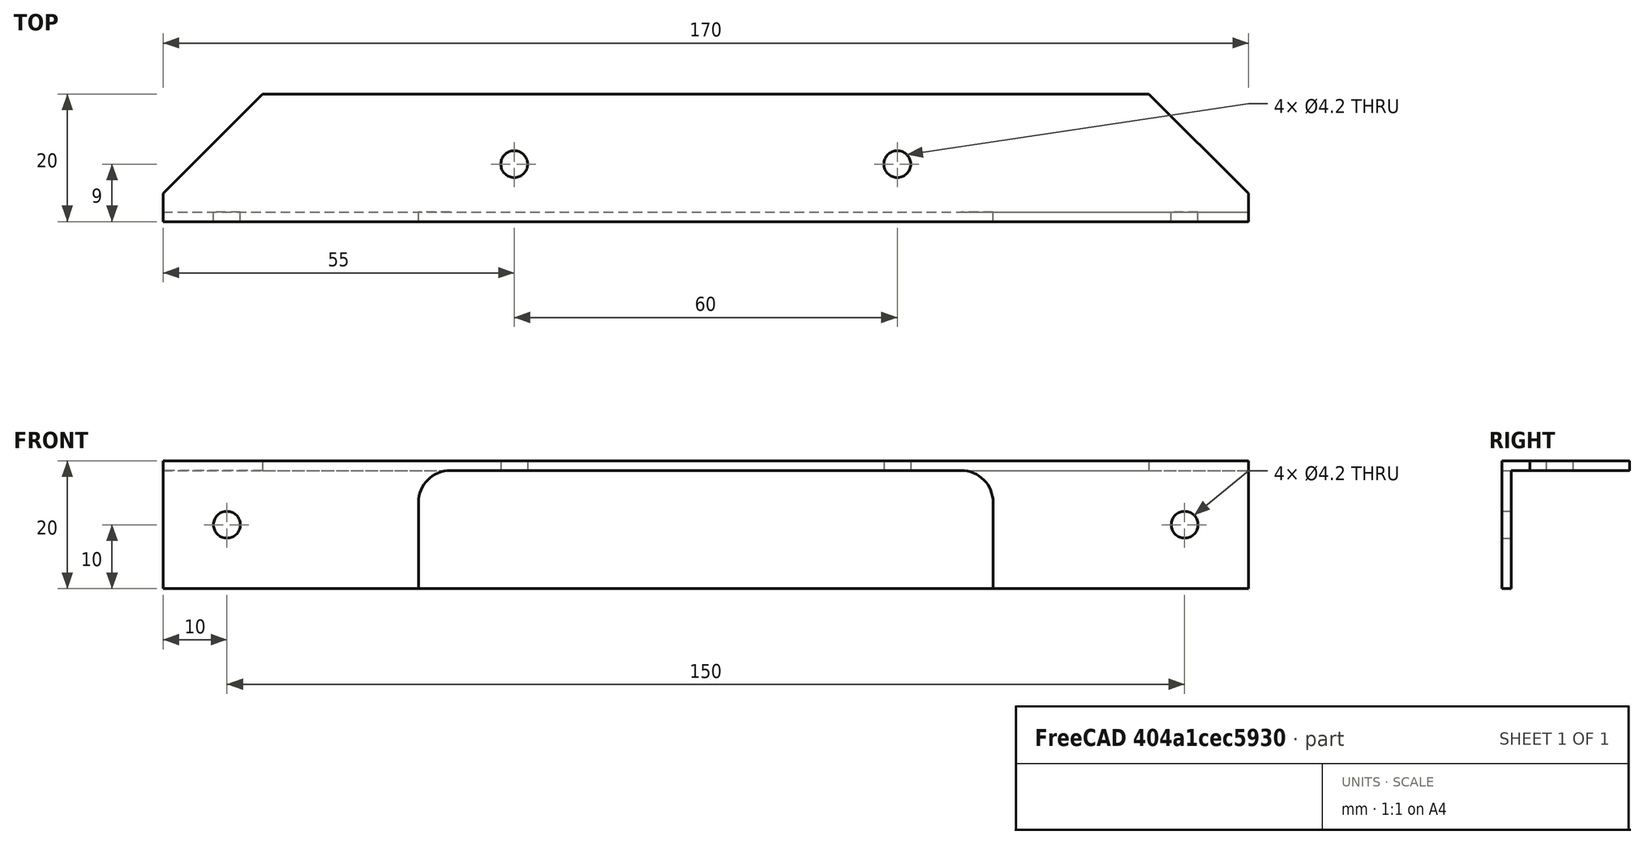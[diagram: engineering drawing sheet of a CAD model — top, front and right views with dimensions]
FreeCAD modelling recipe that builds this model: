
FCSTD DOCUMENT  (FreeCAD 1.0R39319 (Git))
Label: OCT-CPBRC
License: Creative Commons Attribution 4.0
LicenseURL: https://creativecommons.org/licenses/by/4.0/
objects: TechDraw::DrawViewDimension×31, TechDraw::DrawProjGroupItem×6, Sketcher::SketchObject×5, PartDesign::Hole×2, PartDesign::Pocket×2, PartDesign::Body×2, TechDraw::DrawSVGTemplate×2, TechDraw::DrawProjGroup×2, TechDraw::DrawPage×2, PartDesign::Pad×1, PartDesign::FeatureBase×1
note: 80 computed .brp shape members not serialized (recipe doc carries the construction recipe); baked Part::Feature solids carry a one-line shape summary decoded from their .brp

FEATURE [Sketcher::SketchObject] Sketch
  ArcFitTolerance = 1e-06
  AttachmentSupport = -> [YZ_Plane]
  FullyConstrained = true
  MakeInternals = false
  MapMode = 5
  Placement = pos=(0,0,0) rot=(0.57735,0.57735,0.57735;2.0944rad)
  sketch-geometry (6):
    g0: LineSegment StartX=0 StartY=0 StartZ=0 EndX=0 EndY=20 EndZ=0
    g1: LineSegment StartX=0 StartY=20 StartZ=0 EndX=20 EndY=20 EndZ=0
    g2: LineSegment StartX=20 StartY=20 StartZ=0 EndX=20 EndY=18.5 EndZ=0
    g3: LineSegment StartX=20 StartY=18.5 StartZ=0 EndX=1.5 EndY=18.5 EndZ=0
    g4: LineSegment StartX=1.5 StartY=18.5 StartZ=0 EndX=1.5 EndY=0 EndZ=0
    g5: LineSegment StartX=1.5 StartY=0 StartZ=0 EndX=0 EndY=0 EndZ=0
  constraints (17):
    c: Coincident(g-1,g0)
    c: PointOnObject(g0,g-2)
    c: Coincident(g0,g1)
    c: Horizontal(g1)
    c: Coincident(g1,g2)
    c: Coincident(g2,g3)
    c: Horizontal(g3)
    c: Coincident(g3,g4)
    c: PointOnObject(g4,g-1)
    c: Vertical(g4)
    c: Coincident(g4,g5)
    c: Coincident(g5,g0)
    c: Vertical(g2)
    c: DistanceY(g0,g0) = 20
    c: DistanceY(g2,g2) = 1.5
    c: Equal(g5,g2)
    c: DistanceX(g1,g1) = 20
FEATURE [PartDesign::Pad] Pad
  Direction = (1,0,0)
  Length = 170
  Length2 = 10
  Midplane = true
  Placement = pos=(0,0,0) rot=(1,1,1;2.0944rad)
  Profile = -> Sketch
  ReferenceAxis = -> Sketch [N_Axis]
  Suppressed = false
  Type = 0
FEATURE [Sketcher::SketchObject] Sketch001
  ArcFitTolerance = 1e-06
  AttachmentSupport = -> [Pad]
  FullyConstrained = true
  MakeInternals = false
  MapMode = 5
  Placement = pos=(0,2e-16,0) rot=(0.57735,0.57735,-0.57735;2.0944rad)
  sketch-geometry (3):
    g0: Circle CenterX=-10 CenterY=-75 CenterZ=0 NormalX=0 NormalY=0 NormalZ=1 AngleXU=0 Radius=2
    g1: Circle CenterX=-10 CenterY=75 CenterZ=0 NormalX=0 NormalY=0 NormalZ=1 AngleXU=0 Radius=2
    g2: LineSegment [constr] StartX=-10 StartY=-75 StartZ=0 EndX=-10 EndY=75 EndZ=0
  constraints (7):
    c: Coincident(g2,g0)
    c: Coincident(g2,g1)
    c: DistanceY(g2,g2) = 150
    c: Equal(g0,g1)
    c: Diameter(g0) = 4
    c: Distance(g0,g-2) = 10
    c: Symmetric(g0,g1,g-1)
FEATURE [PartDesign::Hole] Hole
  BaseFeature = -> Pad
  CustomThreadClearance = 0
  Depth = 348.12
  DepthType = 1
  Diameter = 4.2
  DrillForDepth = false
  DrillPoint = 1
  DrillPointAngle = 118
  HoleCutCountersinkAngle = 90
  HoleCutCustomValues = false
  HoleCutDepth = 0
  HoleCutDiameter = 6.1
  HoleCutType = 0
  ModelThread = false
  Placement = pos=(0,0,0) rot=(1,1,1;2.0944rad)
  Profile = -> Sketch001
  Suppressed = false
  Tapered = false
  TaperedAngle = 90
  ThreadClass = 0
  ThreadDepth = 348.12
  ThreadDepthType = 0
  ThreadDirection = 0
  ThreadFit = 0
  ThreadSize = 0
  ThreadType = 0
  Threaded = false
  UseCustomThreadClearance = false
FEATURE [Sketcher::SketchObject] Sketch002
  ArcFitTolerance = 1e-06
  AttachmentSupport = -> [Hole]
  FullyConstrained = true
  MakeInternals = false
  MapMode = 5
  Placement = pos=(0,4.4e-15,20) rot=(0,0,-1;1.5708rad)
  sketch-geometry (3):
    g0: Circle CenterX=-9 CenterY=30 CenterZ=0 NormalX=0 NormalY=0 NormalZ=1 AngleXU=0 Radius=2
    g1: Circle CenterX=-9 CenterY=-30 CenterZ=0 NormalX=0 NormalY=0 NormalZ=1 AngleXU=0 Radius=2
    g2: LineSegment [constr] StartX=-9 StartY=30 StartZ=0 EndX=-9 EndY=-30 EndZ=0
  constraints (7):
    c: Coincident(g2,g0)
    c: Coincident(g2,g1)
    c: Symmetric(g1,g0,g-1)
    c: Equal(g0,g1)
    c: Diameter(g1) = 4
    c: DistanceY(g2,g2) = 60
    c: DistanceX(g0,g-1) = 9
FEATURE [PartDesign::Hole] Hole001
  BaseFeature = -> Hole
  CustomThreadClearance = 0
  Depth = 348.12
  DepthType = 1
  Diameter = 4.2
  DrillForDepth = false
  DrillPoint = 1
  DrillPointAngle = 118
  HoleCutCountersinkAngle = 90
  HoleCutCustomValues = false
  HoleCutDepth = 0
  HoleCutDiameter = 6.1
  HoleCutType = 0
  ModelThread = false
  Placement = pos=(0,0,0) rot=(1,1,1;2.0944rad)
  Profile = -> Sketch002
  Suppressed = false
  Tapered = false
  TaperedAngle = 90
  ThreadClass = 0
  ThreadDepth = 348.12
  ThreadDepthType = 0
  ThreadDirection = 0
  ThreadFit = 0
  ThreadSize = 0
  ThreadType = 0
  Threaded = false
  UseCustomThreadClearance = false
FEATURE [Sketcher::SketchObject] Sketch003
  ArcFitTolerance = 1e-06
  AttachmentSupport = -> [Hole001]
  ExternalGeometry = -> [Hole001]
  FullyConstrained = true
  MakeInternals = false
  MapMode = 5
  Placement = pos=(0,4.4e-15,20) rot=(0,0,-1;1.5708rad)
  sketch-geometry (6):
    g0: LineSegment StartX=-4.4 StartY=85 StartZ=0 EndX=-20 EndY=85 EndZ=0
    g1: LineSegment StartX=-20 StartY=85 StartZ=0 EndX=-20 EndY=69.4 EndZ=0
    g2: LineSegment StartX=-20 StartY=69.4 StartZ=0 EndX=-4.4 EndY=85 EndZ=0
    g3: LineSegment StartX=-4.4 StartY=-85 StartZ=0 EndX=-20 EndY=-85 EndZ=0
    g4: LineSegment StartX=-20 StartY=-85 StartZ=0 EndX=-20 EndY=-69.4 EndZ=0
    g5: LineSegment StartX=-20 StartY=-69.4 StartZ=0 EndX=-4.4 EndY=-85 EndZ=0
  constraints (16):
    c: Horizontal(g0)
    c: Coincident(g0,g1)
    c: Vertical(g1)
    c: Coincident(g1,g2)
    c: Coincident(g2,g0)
    c: Horizontal(g3)
    c: Coincident(g3,g4)
    c: Coincident(g4,g5)
    c: Coincident(g5,g3)
    c: Vertical(g4)
    c: Equal(g4,g3)
    c: Equal(g1,g0)
    c: Equal(g1,g4)
    c: Coincident(g0,g-3)
    c: DistanceX(g0,g-3) = 4.4
    c: Symmetric(g0,g3,g-1)
FEATURE [PartDesign::Pocket] Pocket
  BaseFeature = -> Hole001
  Direction = (0,0,-1)
  Length = 5
  Length2 = 5
  Placement = pos=(0,0,0) rot=(1,1,1;2.0944rad)
  Profile = -> Sketch003
  ReferenceAxis = -> Sketch003 [N_Axis]
  Suppressed = false
  Type = 2
FEATURE [PartDesign::Body] Body  label="OCT-CPBRC-AA"
  AllowCompound = false
  Group = -> [Sketch,Pad,Sketch001,Hole,Sketch002,Hole001,Sketch003,Pocket]
  Origin = -> Origin
  Tip = -> Pocket
FEATURE [TechDraw::DrawSVGTemplate] Template
  EditableTexts = approval_person=S. Aphelion; creator=Michael Stoll; date_of_issue=13/02/2026; document_status=In preparation; document_type=Component Drawing; drawing_number=DN; general_tolerances=+-0.1 mm; language_code=EN; part_material=Aluminium; responsible_department=RD; revision_index=A; scale=1 : 1; sheet_number=1 / 1; supplementary_title_1=Chamber Top Bracket; title=OCT-CPBRC-AA
  Height = 297
  Orientation = 1
  Template = C:/Program Files/FreeCAD 1.0/data/Mod/TechDraw/Templates/A3_Landscape_ISO5457_advanced.svg
  Width = 420
FEATURE [TechDraw::DrawProjGroupItem] View  label="Front"
  CoarseView = false
  Direction = (0,-1,0)
  Focus = 100
  HardHidden = false
  IsoCount = 0
  IsoHidden = false
  IsoVisible = false
  LockPosition = true
  Perspective = false
  Rotation = 0
  RotationVector = (1,0,0)
  ScaleType = 2
  ScrubCount = 1
  SeamHidden = false
  SeamVisible = false
  SmoothHidden = false
  SmoothVisible = true
  Source = -> [Body]
  Type = 0
  X = 0
  XDirection = (1,0,0)
  Y = 0
FEATURE [TechDraw::DrawProjGroupItem] ProjItem  label="Top"
  CoarseView = false
  Direction = (0,0,1)
  Focus = 100
  HardHidden = false
  IsoCount = 0
  IsoHidden = false
  IsoVisible = false
  LockPosition = false
  Perspective = false
  Rotation = 0
  RotationVector = (1,0,0)
  ScaleType = 0
  ScrubCount = 1
  SeamHidden = false
  SeamVisible = false
  SmoothHidden = false
  SmoothVisible = true
  Source = -> [Body]
  Type = 4
  X = 0
  XDirection = (1,0,0)
  Y = 70
FEATURE [TechDraw::DrawProjGroupItem] ProjItem001  label="Right"
  CoarseView = false
  Direction = (1,-1e-16,0)
  Focus = 100
  HardHidden = false
  IsoCount = 0
  IsoHidden = false
  IsoVisible = false
  LockPosition = false
  Perspective = false
  Rotation = 0
  RotationVector = (1,0,0)
  ScaleType = 0
  ScrubCount = 1
  SeamHidden = false
  SeamVisible = false
  SmoothHidden = false
  SmoothVisible = true
  Source = -> [Body]
  Type = 2
  X = 145
  XDirection = (1e-16,1,0)
  Y = 0
FEATURE [TechDraw::DrawProjGroup] ProjGroup
  Anchor = -> View
  AutoDistribute = true
  LockPosition = false
  ProjectionType = 1
  Rotation = 0
  ScaleType = 0
  Source = -> [Body]
  Views = -> [View,ProjItem,ProjItem001]
  X = 185.7
  Y = 128.889
  spacingX = 50
  spacingY = 50
FEATURE [TechDraw::DrawViewDimension] Dimension
  AngleOverride = false
  Arbitrary = false
  ArbitraryTolerances = false
  BoxCorners = (2) [(-10,-10,0),(10,10,0)]
  EqualTolerance = true
  ExtensionAngle = 0
  FormatSpec = %.1f
  FormatSpecOverTolerance = %+.1f
  FormatSpecUnderTolerance = %+.1f
  Inverted = false
  LineAngle = 0
  LockPosition = false
  MeasureType = 1
  OverTolerance = 0
  References2D = -> [ProjItem001]
  Rotation = 0
  ScaleType = 0
  TheoreticalExact = false
  Type = 2
  UnderTolerance = 0
  X = -31.2542
  Y = 0
FEATURE [TechDraw::DrawViewDimension] Dimension001
  AngleOverride = false
  Arbitrary = false
  ArbitraryTolerances = false
  BoxCorners = (2) [(-10,-10,0),(10,10,0)]
  EqualTolerance = true
  ExtensionAngle = 0
  FormatSpec = %.1f
  FormatSpecOverTolerance = %+.1f
  FormatSpecUnderTolerance = %+.1f
  Inverted = false
  LineAngle = 0
  LockPosition = false
  MeasureType = 1
  OverTolerance = 0
  References2D = -> [ProjItem001]
  Rotation = 0
  ScaleType = 0
  TheoreticalExact = false
  Type = 1
  UnderTolerance = 0
  X = 0
  Y = 29.0333
FEATURE [TechDraw::DrawViewDimension] Dimension002
  AngleOverride = false
  Arbitrary = false
  ArbitraryTolerances = false
  BoxCorners = (2) [(-10,-10,0),(10,10,0)]
  EqualTolerance = true
  ExtensionAngle = 0
  FormatSpec = %.1f
  FormatSpecOverTolerance = %+.1f
  FormatSpecUnderTolerance = %+.1f
  Inverted = false
  LineAngle = 0
  LockPosition = false
  MeasureType = 1
  OverTolerance = 0
  References2D = -> [ProjItem001]
  Rotation = 0
  ScaleType = 0
  TheoreticalExact = false
  Type = 0
  UnderTolerance = 0
  X = 13.3418
  Y = 21.504
FEATURE [TechDraw::DrawViewDimension] Dimension003
  AngleOverride = false
  Arbitrary = false
  ArbitraryTolerances = false
  BoxCorners = (2) [(-10,-10,0),(10,10,0)]
  EqualTolerance = true
  ExtensionAngle = 0
  FormatSpec = %.1f
  FormatSpecOverTolerance = %+.1f
  FormatSpecUnderTolerance = %+.1f
  Inverted = false
  LineAngle = 0
  LockPosition = false
  MeasureType = 1
  OverTolerance = 0
  References2D = -> [ProjItem001]
  Rotation = 0
  ScaleType = 0
  TheoreticalExact = false
  Type = 0
  UnderTolerance = 0
  X = -22.9044
  Y = -14.5718
FEATURE [TechDraw::DrawViewDimension] Dimension004
  AngleOverride = false
  Arbitrary = false
  ArbitraryTolerances = false
  BoxCorners = (2) [(-85,-10,0),(85,10,0)]
  EqualTolerance = true
  ExtensionAngle = 0
  FormatSpec = %.1f
  FormatSpecOverTolerance = %+.1f
  FormatSpecUnderTolerance = %+.1f
  Inverted = false
  LineAngle = 0
  LockPosition = false
  MeasureType = 1
  OverTolerance = 0
  References2D = -> [ProjItem]
  Rotation = 0
  ScaleType = 0
  TheoreticalExact = false
  Type = 1
  UnderTolerance = 0
  X = 0
  Y = -21.4245
FEATURE [TechDraw::DrawViewDimension] Dimension005
  AngleOverride = false
  Arbitrary = false
  ArbitraryTolerances = false
  BoxCorners = (2) [(-85,-10,0),(85,10,0)]
  EqualTolerance = true
  ExtensionAngle = 0
  FormatSpec = %.1f
  FormatSpecOverTolerance = %+.1f
  FormatSpecUnderTolerance = %+.1f
  Inverted = false
  LineAngle = 0
  LockPosition = false
  MeasureType = 1
  OverTolerance = 0
  References2D = -> [ProjItem]
  Rotation = 0
  ScaleType = 0
  TheoreticalExact = false
  Type = 2
  UnderTolerance = 0
  X = -106.361
  Y = -7.8
FEATURE [TechDraw::DrawViewDimension] Dimension006
  AngleOverride = false
  Arbitrary = false
  ArbitraryTolerances = false
  BoxCorners = (2) [(-85,-10,0),(85,10,0)]
  EqualTolerance = true
  ExtensionAngle = 0
  FormatSpec = %.1f
  FormatSpecOverTolerance = %+.1f
  FormatSpecUnderTolerance = %+.1f
  Inverted = false
  LineAngle = 0
  LockPosition = false
  MeasureType = 1
  OverTolerance = 0
  References2D = -> [ProjItem]
  Rotation = 0
  ScaleType = 0
  TheoreticalExact = false
  Type = 6
  UnderTolerance = 0
  X = -77.4669
  Y = 20.3711
FEATURE [TechDraw::DrawViewDimension] Dimension007
  AngleOverride = false
  Arbitrary = false
  ArbitraryTolerances = false
  BoxCorners = (2) [(-85,-10,0),(85,10,0)]
  EqualTolerance = true
  ExtensionAngle = 0
  FormatSpec = %.1f
  FormatSpecOverTolerance = %+.1f
  FormatSpecUnderTolerance = %+.1f
  Inverted = false
  LineAngle = 0
  LockPosition = false
  MeasureType = 1
  OverTolerance = 0
  References2D = -> [ProjItem]
  Rotation = 0
  ScaleType = 0
  TheoreticalExact = false
  Type = 0
  UnderTolerance = 0
  X = 57.5
  Y = 30.1612
FEATURE [TechDraw::DrawViewDimension] Dimension008
  AngleOverride = false
  Arbitrary = false
  ArbitraryTolerances = false
  BoxCorners = (2) [(-85,-10,0),(85,10,0)]
  EqualTolerance = true
  ExtensionAngle = 0
  FormatSpec = %.1f
  FormatSpecOverTolerance = %+.1f
  FormatSpecUnderTolerance = %+.1f
  Inverted = false
  LineAngle = 0
  LockPosition = false
  MeasureType = 1
  OverTolerance = 0
  References2D = -> [ProjItem]
  Rotation = 0
  ScaleType = 0
  TheoreticalExact = false
  Type = 1
  UnderTolerance = 0
  X = 0
  Y = 30.1612
FEATURE [TechDraw::DrawViewDimension] Dimension009
  AngleOverride = false
  Arbitrary = false
  ArbitraryTolerances = false
  BoxCorners = (2) [(-85,-10,0),(85,10,0)]
  EqualTolerance = true
  ExtensionAngle = 0
  FormatSpec = %.1f
  FormatSpecOverTolerance = %+.1f
  FormatSpecUnderTolerance = %+.1f
  Inverted = false
  LineAngle = 0
  LockPosition = false
  MeasureType = 1
  OverTolerance = 0
  References2D = -> [View]
  Rotation = 0
  ScaleType = 0
  TheoreticalExact = false
  Type = 0
  UnderTolerance = 0
  X = 80
  Y = 29.1973
FEATURE [TechDraw::DrawViewDimension] Dimension010
  AngleOverride = false
  Arbitrary = false
  ArbitraryTolerances = false
  BoxCorners = (2) [(-85,-10,0),(85,10,0)]
  EqualTolerance = true
  ExtensionAngle = 0
  FormatSpec = %.1f
  FormatSpecOverTolerance = %+.1f
  FormatSpecUnderTolerance = %+.1f
  Inverted = false
  LineAngle = 0
  LockPosition = false
  MeasureType = 1
  OverTolerance = 0
  References2D = -> [View]
  Rotation = 0
  ScaleType = 0
  TheoreticalExact = false
  Type = 1
  UnderTolerance = 0
  X = 0
  Y = 29.1973
FEATURE [TechDraw::DrawViewDimension] Dimension011
  AngleOverride = false
  Arbitrary = false
  ArbitraryTolerances = false
  BoxCorners = (2) [(-85,-10,0),(85,10,0)]
  EqualTolerance = true
  ExtensionAngle = 0
  FormatSpec = %.1f
  FormatSpecOverTolerance = %+.1f
  FormatSpecUnderTolerance = %+.1f
  Inverted = false
  LineAngle = 0
  LockPosition = false
  MeasureType = 1
  OverTolerance = 0
  References2D = -> [ProjItem]
  Rotation = 0
  ScaleType = 0
  TheoreticalExact = false
  Type = 0
  UnderTolerance = 0
  X = 115.395
  Y = -5.5
FEATURE [TechDraw::DrawViewDimension] Dimension012
  AngleOverride = false
  Arbitrary = false
  ArbitraryTolerances = false
  BoxCorners = (2) [(-85,-10,0),(85,10,0)]
  EqualTolerance = true
  ExtensionAngle = 0
  FormatSpec = %.1f
  FormatSpecOverTolerance = %+.1f
  FormatSpecUnderTolerance = %+.1f
  Inverted = false
  LineAngle = 0
  LockPosition = false
  MeasureType = 1
  OverTolerance = 0
  References2D = -> [View]
  Rotation = 0
  ScaleType = 0
  TheoreticalExact = false
  Type = 0
  UnderTolerance = 0
  X = 106.675
  Y = 5
FEATURE [TechDraw::DrawViewDimension] Dimension013
  AngleOverride = false
  Arbitrary = false
  ArbitraryTolerances = false
  BoxCorners = (2) [(-85,-10,0),(85,10,0)]
  EqualTolerance = true
  ExtensionAngle = 0
  FormatSpec = ⌀%.1f
  FormatSpecOverTolerance = %+.1f
  FormatSpecUnderTolerance = %+.1f
  Inverted = false
  LineAngle = 0
  LockPosition = false
  MeasureType = 1
  OverTolerance = 0
  References2D = -> [ProjItem]
  Rotation = 0
  ScaleType = 0
  TheoreticalExact = false
  Type = 5
  UnderTolerance = 0
  X = -51.1959
  Y = 35.4634
FEATURE [TechDraw::DrawViewDimension] Dimension014
  AngleOverride = false
  Arbitrary = false
  ArbitraryTolerances = false
  BoxCorners = (2) [(-85,-10,0),(85,10,0)]
  EqualTolerance = true
  ExtensionAngle = 0
  FormatSpec = ⌀%.1f
  FormatSpecOverTolerance = %+.1f
  FormatSpecUnderTolerance = %+.1f
  Inverted = false
  LineAngle = 0
  LockPosition = false
  MeasureType = 1
  OverTolerance = 0
  References2D = -> [View]
  Rotation = 0
  ScaleType = 0
  TheoreticalExact = false
  Type = 5
  UnderTolerance = 0
  X = -114.095
  Y = -17.0735
FEATURE [TechDraw::DrawPage] Page  label="AA"
  KeepUpdated = true
  NextBalloonIndex = 1
  ProjectionType = 1
  Template = -> Template
  Views = -> [ProjGroup,Dimension,Dimension001,Dimension002,Dimension003,Dimension004,Dimension005,Dimension006,Dimension007,Dimension008,Dimension009,Dimension010,Dimension011,Dimension012,Dimension013,Dimension014]
FEATURE [PartDesign::FeatureBase] Clone
  BaseFeature = -> Pocket
  Placement = pos=(0,0,0) rot=(1,1,1;2.0944rad)
  Suppressed = false
FEATURE [Sketcher::SketchObject] Sketch004
  ArcFitTolerance = 1e-06
  AttachmentSupport = -> [XZ_Plane002]
  ExternalGeometry = -> [Clone]
  FullyConstrained = true
  MakeInternals = false
  MapMode = 5
  Placement = pos=(0,0,0) rot=(1,0,0;1.5708rad)
  sketch-geometry (6):
    g0: ArcOfCircle CenterX=-40 CenterY=13.5 CenterZ=0 NormalX=0 NormalY=0 NormalZ=1 AngleXU=0 Radius=5 StartAngle=1.5708 EndAngle=3.14159
    g1: ArcOfCircle CenterX=40 CenterY=13.5 CenterZ=0 NormalX=0 NormalY=0 NormalZ=1 AngleXU=0 Radius=5 StartAngle=0 EndAngle=1.5708
    g2: LineSegment StartX=-40 StartY=18.5 StartZ=0 EndX=40 EndY=18.5 EndZ=0
    g3: LineSegment StartX=-45 StartY=13.5 StartZ=0 EndX=-45 EndY=0 EndZ=0
    g4: LineSegment StartX=-45 StartY=0 StartZ=0 EndX=45 EndY=0 EndZ=0
    g5: LineSegment StartX=45 StartY=0 StartZ=0 EndX=45 EndY=13.5 EndZ=0
  constraints (15):
    c: Tangent(g0,g3) = -1.5708
    c: Coincident(g3,g4)
    c: Horizontal(g4)
    c: Coincident(g4,g5)
    c: Vertical(g5)
    c: Vertical(g3)
    c: Tangent(g2,g0) = 1.5708
    c: Tangent(g5,g1) = -1.5708
    c: Tangent(g2,g1) = 1.5708
    c: Symmetric(g0,g1,g-2)
    c: Equal(g0,g1)
    c: Radius(g0) = 5
    c: PointOnObject(g-3,g2)
    c: PointOnObject(g4,g-1)
    c: DistanceX(g4,g4) = 90
FEATURE [PartDesign::Pocket] Pocket001
  BaseFeature = -> Clone
  Direction = (0,1,-2e-16)
  Length = 5
  Length2 = 5
  Placement = pos=(0,0,0) rot=(1,1,1;2.0944rad)
  Profile = -> Sketch004
  ReferenceAxis = -> Sketch004 [N_Axis]
  Suppressed = false
  Type = 2
FEATURE [PartDesign::Body] Body002  label="OCT-CPBRC-BA"
  AllowCompound = false
  Group = -> [Clone,Sketch004,Pocket001]
  Origin = -> Origin002
  Tip = -> Pocket001
FEATURE [TechDraw::DrawSVGTemplate] Template001
  EditableTexts = approval_person=S. Aphelion; creator=Michael Stoll; date_of_issue=13/02/2026; document_status=In preparation; document_type=Component Drawing; drawing_number=DN; general_tolerances=ISO 2768-m; language_code=EN; part_material=Aluminium; responsible_department=RD; revision_index=A; scale=1 : 1; sheet_number=2 / 2; supplementary_title_1=Chamber Top Bracket, Hinge; title=OCT-CPBRC-BA
  Height = 297
  Orientation = 1
  Template = C:/Program Files/FreeCAD 1.0/data/Mod/TechDraw/Templates/A3_Landscape_ISO5457_advanced.svg
  Width = 420
FEATURE [TechDraw::DrawProjGroupItem] View001  label="Front001"
  CoarseView = false
  Direction = (0,-1,0)
  Focus = 100
  HardHidden = false
  IsoCount = 0
  IsoHidden = false
  IsoVisible = false
  LockPosition = true
  Perspective = false
  Rotation = 0
  RotationVector = (1,0,0)
  ScaleType = 2
  ScrubCount = 1
  SeamHidden = false
  SeamVisible = false
  SmoothHidden = false
  SmoothVisible = true
  Source = -> [Body002]
  Type = 0
  X = 0
  XDirection = (1,0,0)
  Y = 0
FEATURE [TechDraw::DrawProjGroupItem] ProjItem002  label="Top001"
  CoarseView = false
  Direction = (0,0,1)
  Focus = 100
  HardHidden = false
  IsoCount = 0
  IsoHidden = false
  IsoVisible = false
  LockPosition = false
  Perspective = false
  Rotation = 0
  RotationVector = (1,0,0)
  ScaleType = 0
  ScrubCount = 1
  SeamHidden = false
  SeamVisible = false
  SmoothHidden = false
  SmoothVisible = true
  Source = -> [Body002]
  Type = 4
  X = 0
  XDirection = (1,0,0)
  Y = 70
FEATURE [TechDraw::DrawProjGroupItem] ProjItem003  label="Right001"
  CoarseView = false
  Direction = (1,-1e-16,0)
  Focus = 100
  HardHidden = false
  IsoCount = 0
  IsoHidden = false
  IsoVisible = false
  LockPosition = false
  Perspective = false
  Rotation = 0
  RotationVector = (1,0,0)
  ScaleType = 0
  ScrubCount = 1
  SeamHidden = false
  SeamVisible = false
  SmoothHidden = false
  SmoothVisible = true
  Source = -> [Body002]
  Type = 2
  X = 145
  XDirection = (1e-16,1,0)
  Y = 0
FEATURE [TechDraw::DrawProjGroup] ProjGroup001
  Anchor = -> View001
  AutoDistribute = true
  LockPosition = false
  ProjectionType = 1
  Rotation = 0
  ScaleType = 0
  Source = -> [Body002]
  Views = -> [View001,ProjItem002,ProjItem003]
  X = 179.346
  Y = 143.102
  spacingX = 50
  spacingY = 50
FEATURE [TechDraw::DrawViewDimension] Dimension015
  AngleOverride = false
  Arbitrary = false
  ArbitraryTolerances = false
  BoxCorners = (2) [(-85,-10,0),(85,10,0)]
  EqualTolerance = true
  ExtensionAngle = 0
  FormatSpec = %.1f
  FormatSpecOverTolerance = %+.1f
  FormatSpecUnderTolerance = %+.1f
  Inverted = false
  LineAngle = 0
  LockPosition = false
  MeasureType = 1
  OverTolerance = 0
  References2D = -> [ProjItem002]
  Rotation = 0
  ScaleType = 0
  TheoreticalExact = false
  Type = 2
  UnderTolerance = 0
  X = -120.051
  Y = -7.8
FEATURE [TechDraw::DrawViewDimension] Dimension018
  AngleOverride = false
  Arbitrary = false
  ArbitraryTolerances = false
  BoxCorners = (2) [(-85,-10,0),(85,10,0)]
  EqualTolerance = true
  ExtensionAngle = 0
  FormatSpec = %.1f
  FormatSpecOverTolerance = %+.1f
  FormatSpecUnderTolerance = %+.1f
  Inverted = false
  LineAngle = 0
  LockPosition = false
  MeasureType = 1
  OverTolerance = 0
  References2D = -> [View001]
  Rotation = 0
  ScaleType = 0
  TheoreticalExact = false
  Type = 1
  UnderTolerance = 0
  X = 0
  Y = 27.0324
FEATURE [TechDraw::DrawViewDimension] Dimension019
  AngleOverride = false
  Arbitrary = false
  ArbitraryTolerances = false
  BoxCorners = (2) [(-10,-10,0),(10,10,0)]
  EqualTolerance = true
  ExtensionAngle = 0
  FormatSpec = %.1f
  FormatSpecOverTolerance = %+.1f
  FormatSpecUnderTolerance = %+.1f
  Inverted = false
  LineAngle = 0
  LockPosition = false
  MeasureType = 1
  OverTolerance = 0
  References2D = -> [ProjItem003]
  Rotation = 0
  ScaleType = 0
  TheoreticalExact = false
  Type = 1
  UnderTolerance = 0
  X = 0
  Y = 28.7316
FEATURE [TechDraw::DrawViewDimension] Dimension020
  AngleOverride = false
  Arbitrary = false
  ArbitraryTolerances = false
  BoxCorners = (2) [(-10,-10,0),(10,10,0)]
  EqualTolerance = true
  ExtensionAngle = 0
  FormatSpec = %.1f
  FormatSpecOverTolerance = %+.1f
  FormatSpecUnderTolerance = %+.1f
  Inverted = false
  LineAngle = 0
  LockPosition = false
  MeasureType = 1
  OverTolerance = 0
  References2D = -> [ProjItem003]
  Rotation = 0
  ScaleType = 0
  TheoreticalExact = false
  Type = 2
  UnderTolerance = 0
  X = -28.6473
  Y = 0
FEATURE [TechDraw::DrawViewDimension] Dimension021
  AngleOverride = false
  Arbitrary = false
  ArbitraryTolerances = false
  BoxCorners = (2) [(-10,-10,0),(10,10,0)]
  EqualTolerance = true
  ExtensionAngle = 0
  FormatSpec = %.1f
  FormatSpecOverTolerance = %+.1f
  FormatSpecUnderTolerance = %+.1f
  Inverted = false
  LineAngle = 0
  LockPosition = false
  MeasureType = 1
  OverTolerance = 0
  References2D = -> [ProjItem003]
  Rotation = 0
  ScaleType = 0
  TheoreticalExact = false
  Type = 0
  UnderTolerance = 0
  X = -2.03802
  Y = -21.3158
FEATURE [TechDraw::DrawViewDimension] Dimension022
  AngleOverride = false
  Arbitrary = false
  ArbitraryTolerances = false
  BoxCorners = (2) [(-10,-10,0),(10,10,0)]
  EqualTolerance = true
  ExtensionAngle = 0
  FormatSpec = %.1f
  FormatSpecOverTolerance = %+.1f
  FormatSpecUnderTolerance = %+.1f
  Inverted = false
  LineAngle = 0
  LockPosition = false
  MeasureType = 1
  OverTolerance = 0
  References2D = -> [ProjItem003]
  Rotation = 0
  ScaleType = 0
  TheoreticalExact = false
  Type = 0
  UnderTolerance = 0
  X = 29.8789
  Y = 9.25
FEATURE [TechDraw::DrawViewDimension] Dimension023
  AngleOverride = false
  Arbitrary = false
  ArbitraryTolerances = false
  BoxCorners = (2) [(-85,-10,0),(85,10,0)]
  EqualTolerance = true
  ExtensionAngle = 0
  FormatSpec = %.1f
  FormatSpecOverTolerance = %+.1f
  FormatSpecUnderTolerance = %+.1f
  Inverted = false
  LineAngle = 0
  LockPosition = false
  MeasureType = 1
  OverTolerance = 0
  References2D = -> [View001]
  Rotation = 0
  ScaleType = 0
  TheoreticalExact = false
  Type = 0
  UnderTolerance = 0
  X = 107.937
  Y = 5
FEATURE [TechDraw::DrawViewDimension] Dimension024
  AngleOverride = false
  Arbitrary = false
  ArbitraryTolerances = false
  BoxCorners = (2) [(-85,-10,0),(85,10,0)]
  EqualTolerance = true
  ExtensionAngle = 0
  FormatSpec = %.1f
  FormatSpecOverTolerance = %+.1f
  FormatSpecUnderTolerance = %+.1f
  Inverted = false
  LineAngle = 0
  LockPosition = false
  MeasureType = 1
  OverTolerance = 0
  References2D = -> [View001]
  Rotation = 0
  ScaleType = 0
  TheoreticalExact = false
  Type = 1
  UnderTolerance = 0
  X = 0
  Y = -34.4832
FEATURE [TechDraw::DrawViewDimension] Dimension025
  AngleOverride = false
  Arbitrary = false
  ArbitraryTolerances = false
  BoxCorners = (2) [(-85,-10,0),(85,10,0)]
  EqualTolerance = true
  ExtensionAngle = 0
  FormatSpec = %.1f
  FormatSpecOverTolerance = %+.1f
  FormatSpecUnderTolerance = %+.1f
  Inverted = false
  LineAngle = 0
  LockPosition = false
  MeasureType = 1
  OverTolerance = 0
  References2D = -> [View001]
  Rotation = 0
  ScaleType = 0
  TheoreticalExact = false
  Type = 2
  UnderTolerance = 0
  X = -102.664
  Y = -0.75
FEATURE [TechDraw::DrawViewDimension] Dimension026
  AngleOverride = false
  Arbitrary = false
  ArbitraryTolerances = false
  BoxCorners = (2) [(-85,-10,0),(85,10,0)]
  EqualTolerance = true
  ExtensionAngle = 0
  FormatSpec = R%.1f
  FormatSpecOverTolerance = %+.1f
  FormatSpecUnderTolerance = %+.1f
  Inverted = false
  LineAngle = 0
  LockPosition = false
  MeasureType = 1
  OverTolerance = 0
  References2D = -> [View001]
  Rotation = 0
  ScaleType = 0
  TheoreticalExact = false
  Type = 4
  UnderTolerance = 0
  X = 9.05367
  Y = 1.82109
FEATURE [TechDraw::DrawViewDimension] Dimension027
  AngleOverride = false
  Arbitrary = false
  ArbitraryTolerances = false
  BoxCorners = (2) [(-85,-10,0),(85,10,0)]
  EqualTolerance = true
  ExtensionAngle = 0
  FormatSpec = %.1f
  FormatSpecOverTolerance = %+.1f
  FormatSpecUnderTolerance = %+.1f
  Inverted = false
  LineAngle = 0
  LockPosition = false
  MeasureType = 1
  OverTolerance = 0
  References2D = -> [View001]
  Rotation = 0
  ScaleType = 0
  TheoreticalExact = false
  Type = 1
  UnderTolerance = 0
  X = 0
  Y = -22.9706
FEATURE [TechDraw::DrawViewDimension] Dimension028
  AngleOverride = false
  Arbitrary = false
  ArbitraryTolerances = false
  BoxCorners = (2) [(-85,-10,0),(85,10,0)]
  EqualTolerance = true
  ExtensionAngle = 0
  FormatSpec = %.1f
  FormatSpecOverTolerance = %+.1f
  FormatSpecUnderTolerance = %+.1f
  Inverted = false
  LineAngle = 0
  LockPosition = false
  MeasureType = 1
  OverTolerance = 0
  References2D = -> [ProjItem002]
  Rotation = 0
  ScaleType = 0
  TheoreticalExact = false
  Type = 1
  UnderTolerance = 0
  X = 0
  Y = 31.9128
FEATURE [TechDraw::DrawViewDimension] Dimension029
  AngleOverride = false
  Arbitrary = false
  ArbitraryTolerances = false
  BoxCorners = (2) [(-85,-10,0),(85,10,0)]
  EqualTolerance = true
  ExtensionAngle = 0
  FormatSpec = %.1f
  FormatSpecOverTolerance = %+.1f
  FormatSpecUnderTolerance = %+.1f
  Inverted = false
  LineAngle = 0
  LockPosition = false
  MeasureType = 1
  OverTolerance = 0
  References2D = -> [ProjItem002]
  Rotation = 0
  ScaleType = 0
  TheoreticalExact = false
  Type = 0
  UnderTolerance = 0
  X = -57.5
  Y = 31.9128
FEATURE [TechDraw::DrawViewDimension] Dimension030
  AngleOverride = false
  Arbitrary = false
  ArbitraryTolerances = false
  BoxCorners = (2) [(-85,-10,0),(85,10,0)]
  EqualTolerance = true
  ExtensionAngle = 0
  FormatSpec = %.1f
  FormatSpecOverTolerance = %+.1f
  FormatSpecUnderTolerance = %+.1f
  Inverted = false
  LineAngle = 0
  LockPosition = false
  MeasureType = 1
  OverTolerance = 0
  References2D = -> [ProjItem002]
  Rotation = 0
  ScaleType = 0
  TheoreticalExact = false
  Type = 6
  UnderTolerance = 0
  X = 55.4931
  Y = 29.6462
FEATURE [TechDraw::DrawViewDimension] Dimension031
  AngleOverride = false
  Arbitrary = false
  ArbitraryTolerances = false
  BoxCorners = (2) [(-85,-10,0),(85,10,0)]
  EqualTolerance = true
  ExtensionAngle = 0
  FormatSpec = %.1f
  FormatSpecOverTolerance = %+.1f
  FormatSpecUnderTolerance = %+.1f
  Inverted = false
  LineAngle = 0
  LockPosition = false
  MeasureType = 1
  OverTolerance = 0
  References2D = -> [ProjItem002]
  Rotation = 0
  ScaleType = 0
  TheoreticalExact = false
  Type = 0
  UnderTolerance = 0
  X = 109.74
  Y = -5.5
FEATURE [TechDraw::DrawViewDimension] Dimension032
  AngleOverride = false
  Arbitrary = false
  ArbitraryTolerances = false
  BoxCorners = (2) [(-85,-10,0),(85,10,0)]
  EqualTolerance = true
  ExtensionAngle = 0
  FormatSpec = %.1f
  FormatSpecOverTolerance = %+.1f
  FormatSpecUnderTolerance = %+.1f
  Inverted = false
  LineAngle = 0
  LockPosition = false
  MeasureType = 1
  OverTolerance = 0
  References2D = -> [View001]
  Rotation = 0
  ScaleType = 0
  TheoreticalExact = false
  Type = 0
  UnderTolerance = 0
  X = -80
  Y = -34.4832
FEATURE [TechDraw::DrawPage] Page001
  KeepUpdated = true
  NextBalloonIndex = 1
  ProjectionType = 1
  Template = -> Template001
  Views = -> [ProjGroup001,Dimension015,Dimension018,Dimension019,Dimension020,Dimension021,Dimension022,Dimension023,Dimension024,Dimension025,Dimension026,Dimension027,Dimension028,Dimension029,Dimension030,Dimension031,Dimension032]
